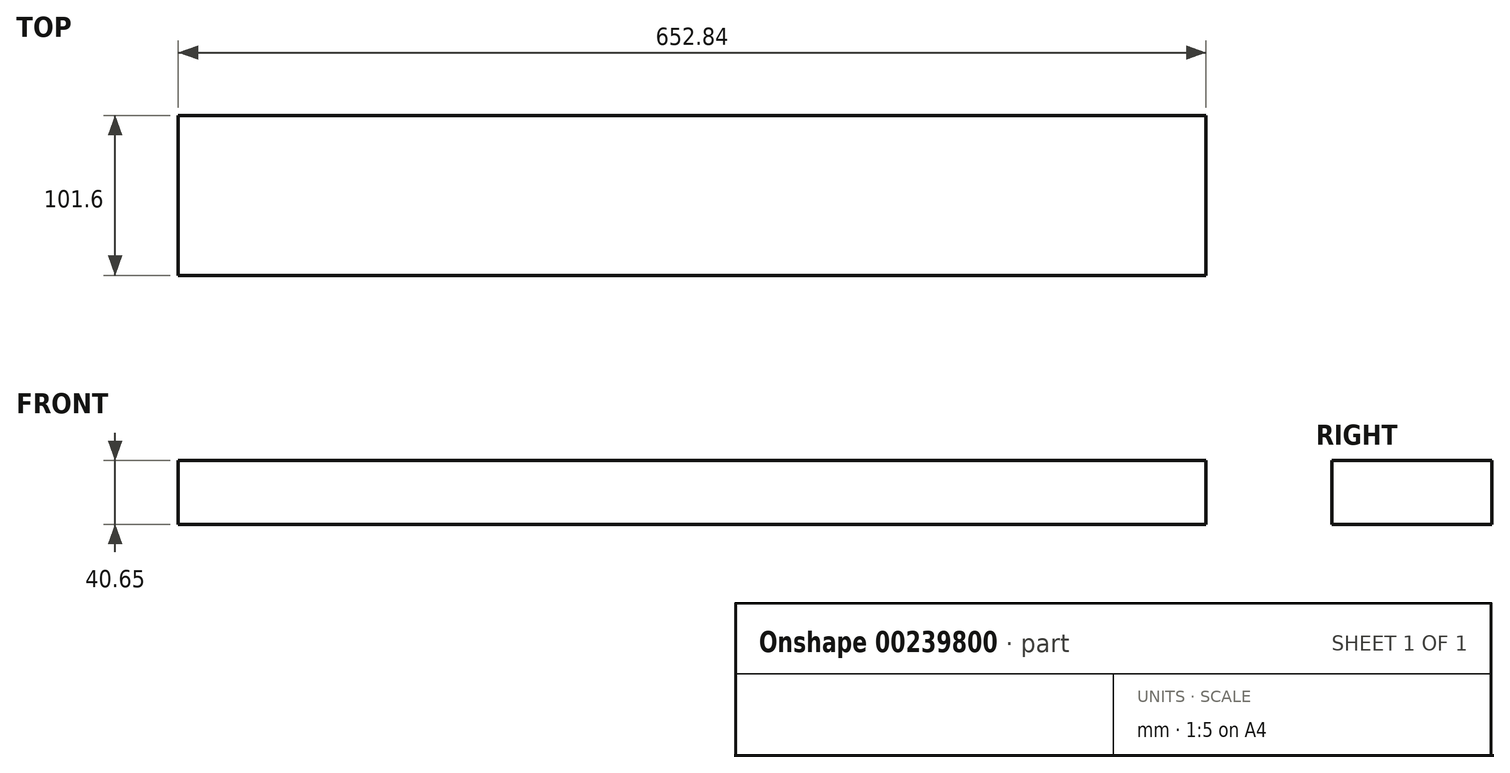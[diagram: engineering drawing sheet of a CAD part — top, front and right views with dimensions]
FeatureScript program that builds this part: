
annotation { "Feature Type Name" : "Feature", "Feature Type Description" : "" }
export const myFeature = defineFeature(function(context is Context, id is Id, definition is map)
    precondition{}
    {
        {
            var Q0;
            Q0=qCreatedBy(makeId("Front.planeOp"),FACE);
            var sketch = newSketch(context, id + "F0", { "sketchPlane" : qUnion([Q0])});
            skLineSegment(sketch, "E0.bottom", {"start": v(-375.27, -63.93) * mm, "end": v(277.57, -63.93) * mm});
            skLineSegment(sketch, "E0.top", {"start": v(-375.27, -23.28) * mm, "end": v(277.57, -23.28) * mm});
            skLineSegment(sketch, "E0.left", {"start": v(-375.27, -63.93) * mm, "end": v(-375.27, -23.28) * mm});
            skLineSegment(sketch, "E0.right", {"start": v(277.57, -63.93) * mm, "end": v(277.57, -23.28) * mm});
            skSolve(sketch);
        }
        {
            var Q0;
            Q0=makeQuery(id+"F0.imprint","IMPRINT",FACE,{"disambiguationData":[TD([[makeQuery(id+"F0.imprint","IMPRINT",EDGE,{"derivedFrom":sQuery(id+"F0.wireOp",EDGE,"E0.bottom")}),1.0]])]});
            extrude(context, id + "F1", {"entities" : qUnion([Q0]), "depth" : 101.6 * mm});
        }
    });
